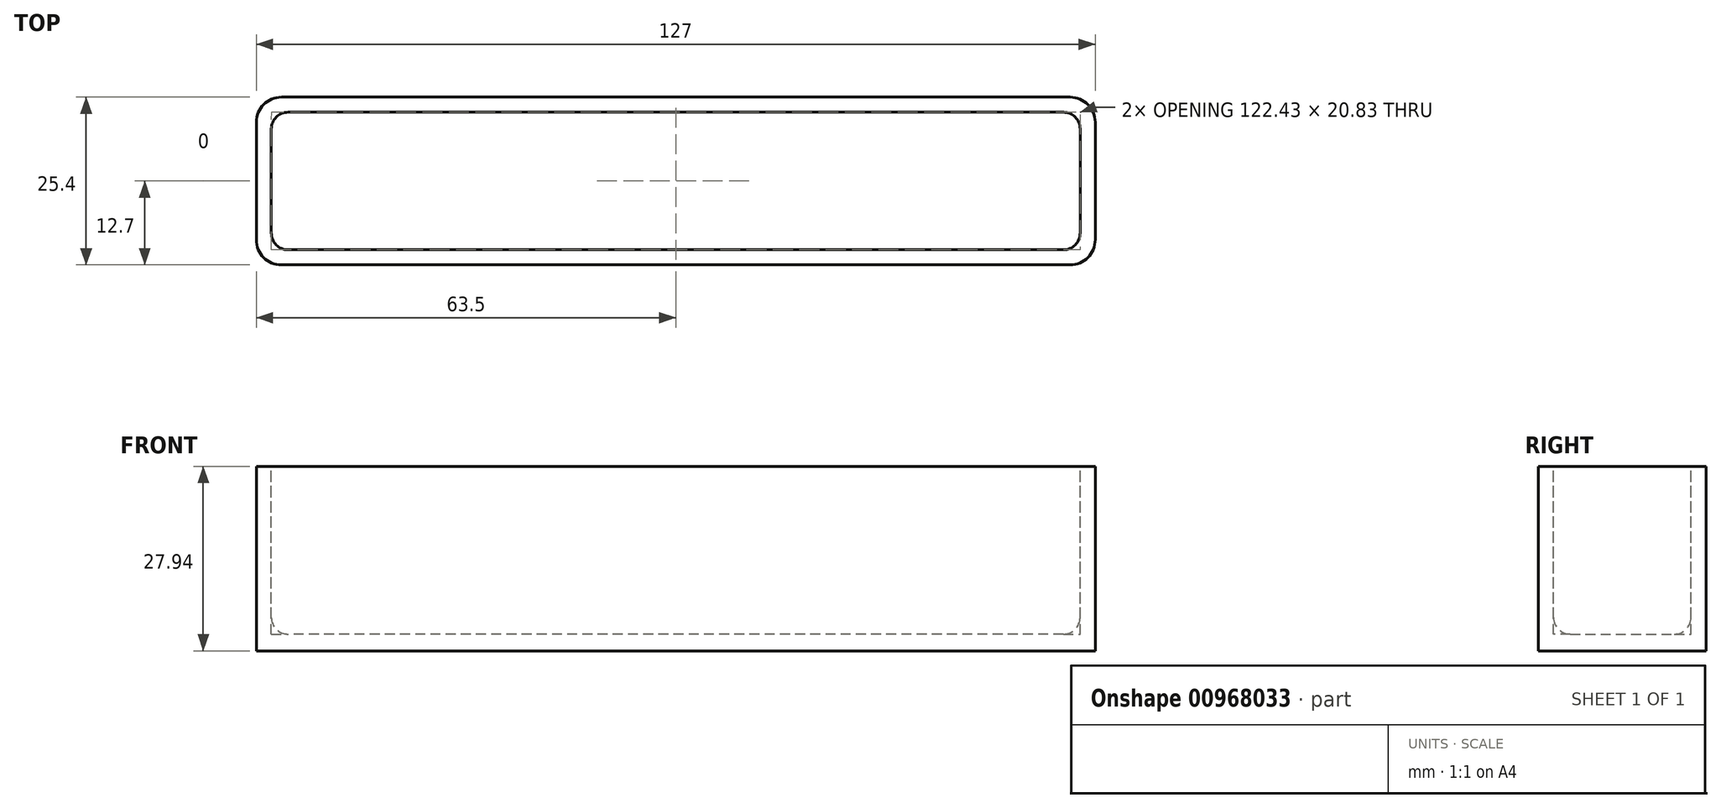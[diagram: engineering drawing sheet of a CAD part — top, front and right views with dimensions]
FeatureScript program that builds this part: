
annotation { "Feature Type Name" : "Feature", "Feature Type Description" : "" }
export const myFeature = defineFeature(function(context is Context, id is Id, definition is map)
    precondition{}
    {
        {
            var Q0;
            Q0=qCreatedBy(makeId("Top.planeOp"),FACE);
            var sketch = newSketch(context, id + "F0", { "sketchPlane" : qUnion([Q0])});
            skLineSegment(sketch, "E0.bottom", {"start": v(63.5, -12.7) * mm, "end": v(-63.5, -12.7) * mm});
            skLineSegment(sketch, "E0.top", {"start": v(63.5, 12.7) * mm, "end": v(-63.5, 12.7) * mm});
            skLineSegment(sketch, "E0.left", {"start": v(63.5, -12.7) * mm, "end": v(63.5, 12.7) * mm});
            skLineSegment(sketch, "E0.right", {"start": v(-63.5, -12.7) * mm, "end": v(-63.5, 12.7) * mm});
            skPoint(sketch, "E0.middle", {"position": v(0, 0) * mm});
            skSolve(sketch);
        }
        {
            var Q0;
            Q0=makeQuery(id+"F0.imprint","IMPRINT",FACE,{"disambiguationData":[TD([[makeQuery(id+"F0.imprint","IMPRINT",EDGE,{"derivedFrom":sQuery(id+"F0.wireOp",EDGE,"E0.bottom")}),-1.0]])]});
            extrude(context, id + "F1", {"entities" : qUnion([Q0]), "depth" : 27.94 * mm, "offsetDistance" : 25.4 * mm});
        }
        {
            var Q0;
            Q0=makeQuery(id+"F1.opExtrude","CAP_FACE",FACE,{"disambiguationData":[OSD([sQuery(id+"F0.wireOp",EDGE,"E0.bottom"),sQuery(id+"F0.wireOp",EDGE,"E0.top"),sQuery(id+"F0.wireOp",EDGE,"E0.left"),sQuery(id+"F0.wireOp",EDGE,"E0.right")])],"isStart":false});
            var sketch = newSketch(context, id + "F2", { "sketchPlane" : qUnion([Q0])});
            skLineSegment(sketch, "E1.0", {"start": v(61.21, -10.41) * mm, "end": v(61.21, 10.41) * mm});
            skLineSegment(sketch, "E1.1", {"start": v(-61.21, -10.41) * mm, "end": v(61.21, -10.41) * mm});
            skLineSegment(sketch, "E1.2", {"start": v(-61.21, 10.41) * mm, "end": v(-61.21, -10.41) * mm});
            skLineSegment(sketch, "E1.3", {"start": v(61.21, 10.41) * mm, "end": v(-61.21, 10.41) * mm});
            skSolve(sketch);
        }
        {
            var Q0;
            Q0=makeQuery(id+"F2.imprint","IMPRINT",FACE,{"disambiguationData":[TD([[makeQuery(id+"F2.imprint","IMPRINT",EDGE,{"derivedFrom":sQuery(id+"F2.wireOp",EDGE,"E1.0")}),1.0]])]});
            extrude(context, id + "F3", {"entities" : qUnion([Q0]), "operationType" : NewBodyOperationType.REMOVE, "oppositeDirection" : true, "depth" : 25.4 * mm, "offsetDistance" : 25.4 * mm});
        }
        {
            var Q0;
            Q0=makeQuery(id+"F3.boolean.opBoolean","COPY",FACE,{"derivedFrom":makeQuery(id+"F3.opExtrude","CAP_FACE",FACE,{"disambiguationData":[OSD([sQuery(id+"F2.wireOp",EDGE,"E1.0"),sQuery(id+"F2.wireOp",EDGE,"E1.1"),sQuery(id+"F2.wireOp",EDGE,"E1.2"),sQuery(id+"F2.wireOp",EDGE,"E1.3")])],"isStart":false})});
            var Q1;
            Q1=makeQuery(id+"F3.boolean.opBoolean","COPY",EDGE,{"derivedFrom":makeQuery(id+"F3.opExtrude","SWEPT_EDGE",EDGE,{"disambiguationData":[OSD([sQuery(id+"F2.wireOp",EDGE,"E1.2"),sQuery(id+"F2.wireOp",EDGE,"E1.3")])]})});
            var Q2;
            Q2=makeQuery(id+"F3.boolean.opBoolean","COPY",EDGE,{"derivedFrom":makeQuery(id+"F3.opExtrude","SWEPT_EDGE",EDGE,{"disambiguationData":[OSD([sQuery(id+"F2.wireOp",EDGE,"E1.0"),sQuery(id+"F2.wireOp",EDGE,"E1.3")])]})});
            var Q3;
            Q3=makeQuery(id+"F3.boolean.opBoolean","COPY",EDGE,{"derivedFrom":makeQuery(id+"F3.opExtrude","SWEPT_EDGE",EDGE,{"disambiguationData":[OSD([sQuery(id+"F2.wireOp",EDGE,"E1.0"),sQuery(id+"F2.wireOp",EDGE,"E1.1")])]})});
            var Q4;
            Q4=makeQuery(id+"F3.boolean.opBoolean","COPY",EDGE,{"derivedFrom":makeQuery(id+"F3.opExtrude","SWEPT_EDGE",EDGE,{"disambiguationData":[OSD([sQuery(id+"F2.wireOp",EDGE,"E1.1"),sQuery(id+"F2.wireOp",EDGE,"E1.2")])]})});
            fillet(context, id + "F4", {"entities" : qUnion([Q0, Q1, Q2, Q3, Q4]), "radius" : 2.54 * mm, "tangentPropagation" : true, "allowEdgeOverflow" : false});
        }
        {
            var Q0;
            Q0=makeQuery(id+"F1.opExtrude","SWEPT_EDGE",EDGE,{"disambiguationData":[OSD([sQuery(id+"F0.wireOp",EDGE,"E0.bottom"),sQuery(id+"F0.wireOp",EDGE,"E0.right")])]});
            var Q1;
            Q1=makeQuery(id+"F1.opExtrude","SWEPT_EDGE",EDGE,{"disambiguationData":[OSD([sQuery(id+"F0.wireOp",EDGE,"E0.top"),sQuery(id+"F0.wireOp",EDGE,"E0.right")])]});
            var Q2;
            Q2=makeQuery(id+"F1.opExtrude","SWEPT_EDGE",EDGE,{"disambiguationData":[OSD([sQuery(id+"F0.wireOp",EDGE,"E0.top"),sQuery(id+"F0.wireOp",EDGE,"E0.left")])]});
            var Q3;
            Q3=makeQuery(id+"F1.opExtrude","SWEPT_EDGE",EDGE,{"disambiguationData":[OSD([sQuery(id+"F0.wireOp",EDGE,"E0.bottom"),sQuery(id+"F0.wireOp",EDGE,"E0.left")])]});
            fillet(context, id + "F5", {"entities" : qUnion([Q0, Q1, Q2, Q3]), "radius" : 3.8 * mm, "tangentPropagation" : true, "allowEdgeOverflow" : false});
        }
    });
